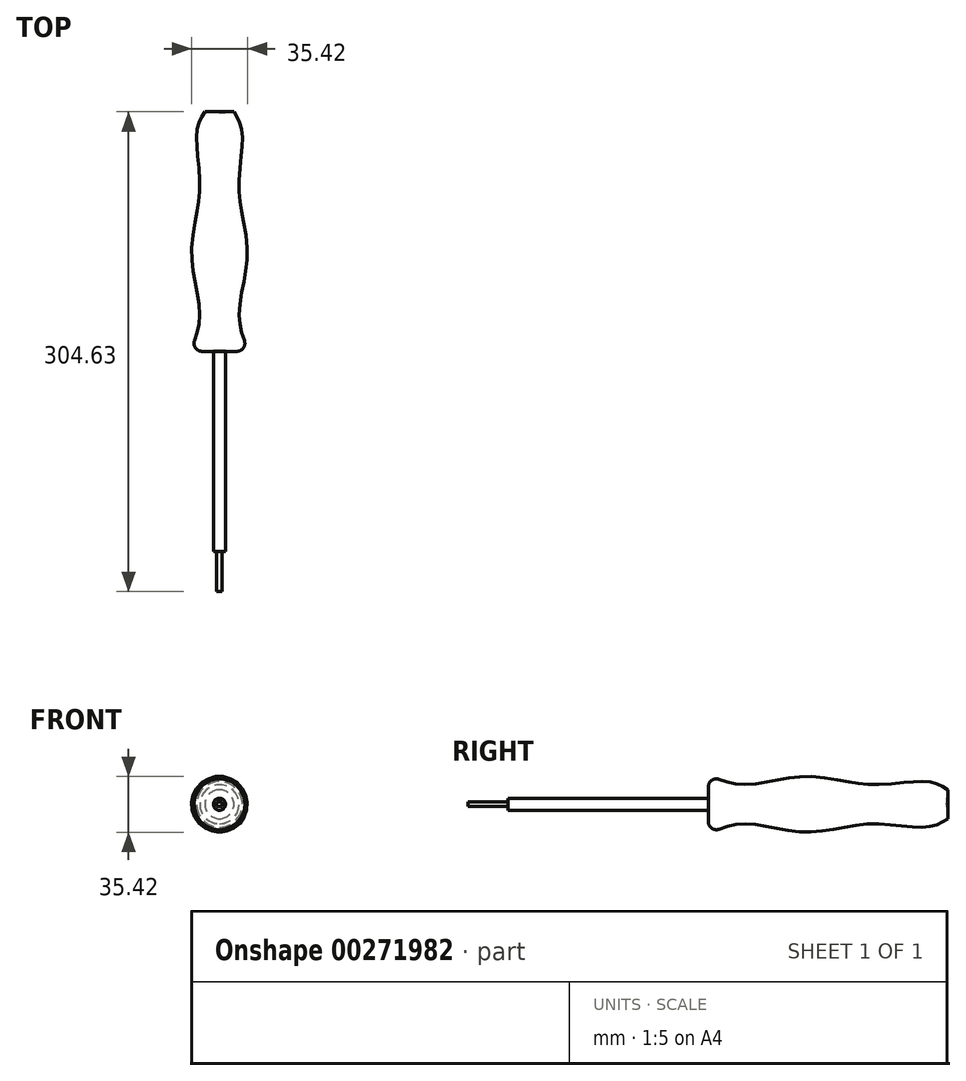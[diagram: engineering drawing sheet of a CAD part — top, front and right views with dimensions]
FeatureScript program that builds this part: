
annotation { "Feature Type Name" : "Feature", "Feature Type Description" : "" }
export const myFeature = defineFeature(function(context is Context, id is Id, definition is map)
    precondition{}
    {
        {
            var Q0;
            Q0=qCreatedBy(makeId("Right.planeOp"),FACE);
            var sketch = newSketch(context, id + "F0", { "sketchPlane" : qUnion([Q0])});
            skLineSegment(sketch, "E0", {"start": v(-75.48, 0) * mm, "end": v(75.2, 0) * mm, "construction": true});
            skFitSpline(sketch, "E1", {"points": [v(-76.58, 18.8) * mm, v(-52.7, 12.49) * mm, v(-14.27, 17.7) * mm, v(26.9, 12.49) * mm, v(62.86, 14.41) * mm, v(76.03, 9.2) * mm], "startDerivative": vector(122.91, -52.3) * mm, "endDerivative": vector(82.14, -50.35) * mm});
            skLineSegment(sketch, "E2", {"start": v(-76.58, 18.8) * mm, "end": v(-75.48, 0) * mm});
            skLineSegment(sketch, "E3", {"start": v(76.03, 9.2) * mm, "end": v(75.2, 0) * mm});
            skLineSegment(sketch, "E4", {"start": v(-75.48, 0) * mm, "end": v(75.2, 0) * mm});
            skSolve(sketch);
        }
        {
            var Q0;
            Q0=makeQuery(id+"F0.imprint","IMPRINT",FACE,{"disambiguationData":[TD([[makeQuery(id+"F0.imprint","IMPRINT",EDGE,{"derivedFrom":sQuery(id+"F0.wireOp",EDGE,"E1")}),-1.0]])]});
            var Q1;
            Q1=sQuery(id+"F0.wireOp",EDGE,"E4");
            revolve(context, id + "F1", {"entities" : qUnion([Q0]), "axis" : qUnion([Q1]), "revolveType" : RevolveType.FULL});
        }
        {
            var Q0;
            Q0=qCreatedBy(makeId("Front.planeOp"),FACE);
            var sketch = newSketch(context, id + "F2", { "sketchPlane" : qUnion([Q0])});
            skCircle(sketch, "E5", {"center": v(0, 0) * mm, "radius": 3.86 * mm});
            skSolve(sketch);
        }
        {
            var Q0;
            Q0 = qSketchRegion(id + "F2", true);
            extrude(context, id + "F3", {"entities" : qUnion([Q0]), "operationType" : NewBodyOperationType.ADD, "depth" : 203.2 * mm});
        }
        {
            var Q0;
            Q0=makeQuery(id+"F1.opRevolve","SWEPT_EDGE",EDGE,{"disambiguationData":[OSD([sQuery(id+"F0.wireOp",EDGE,"E1"),sQuery(id+"F0.wireOp",EDGE,"E2")])]});
            fillet(context, id + "F4", {"entities" : qUnion([Q0]), "radius" : 5.08 * mm, "tangentPropagation" : true, "allowEdgeOverflow" : false});
        }
        {
            var Q0;
            Q0=makeQuery(id+"F3.opExtrude","CAP_FACE",FACE,{"disambiguationData":[OSD([sQuery(id+"F2.wireOp",EDGE,"E5")])],"isStart":false});
            var sketch = newSketch(context, id + "F5", { "sketchPlane" : qUnion([Q0])});
            skLineSegment(sketch, "E6.bottom", {"start": v(1.79, -1.44) * mm, "end": v(-1.79, -1.44) * mm});
            skLineSegment(sketch, "E6.top", {"start": v(1.79, 1.44) * mm, "end": v(-1.79, 1.44) * mm});
            skLineSegment(sketch, "E6.left", {"start": v(1.79, -1.44) * mm, "end": v(1.79, 1.44) * mm});
            skLineSegment(sketch, "E6.right", {"start": v(-1.79, -1.44) * mm, "end": v(-1.79, 1.44) * mm});
            skPoint(sketch, "E6.middle", {"position": v(0, 0) * mm});
            skSolve(sketch);
        }
        {
            var Q0;
            Q0=makeQuery(id+"F5.imprint","IMPRINT",FACE,{"disambiguationData":[TD([[makeQuery(id+"F5.imprint","IMPRINT",EDGE,{"derivedFrom":sQuery(id+"F5.wireOp",EDGE,"E6.bottom")}),-1.0]])]});
            extrude(context, id + "F6", {"entities" : qUnion([Q0]), "operationType" : NewBodyOperationType.ADD, "depth" : 25.4 * mm});
        }
    });
